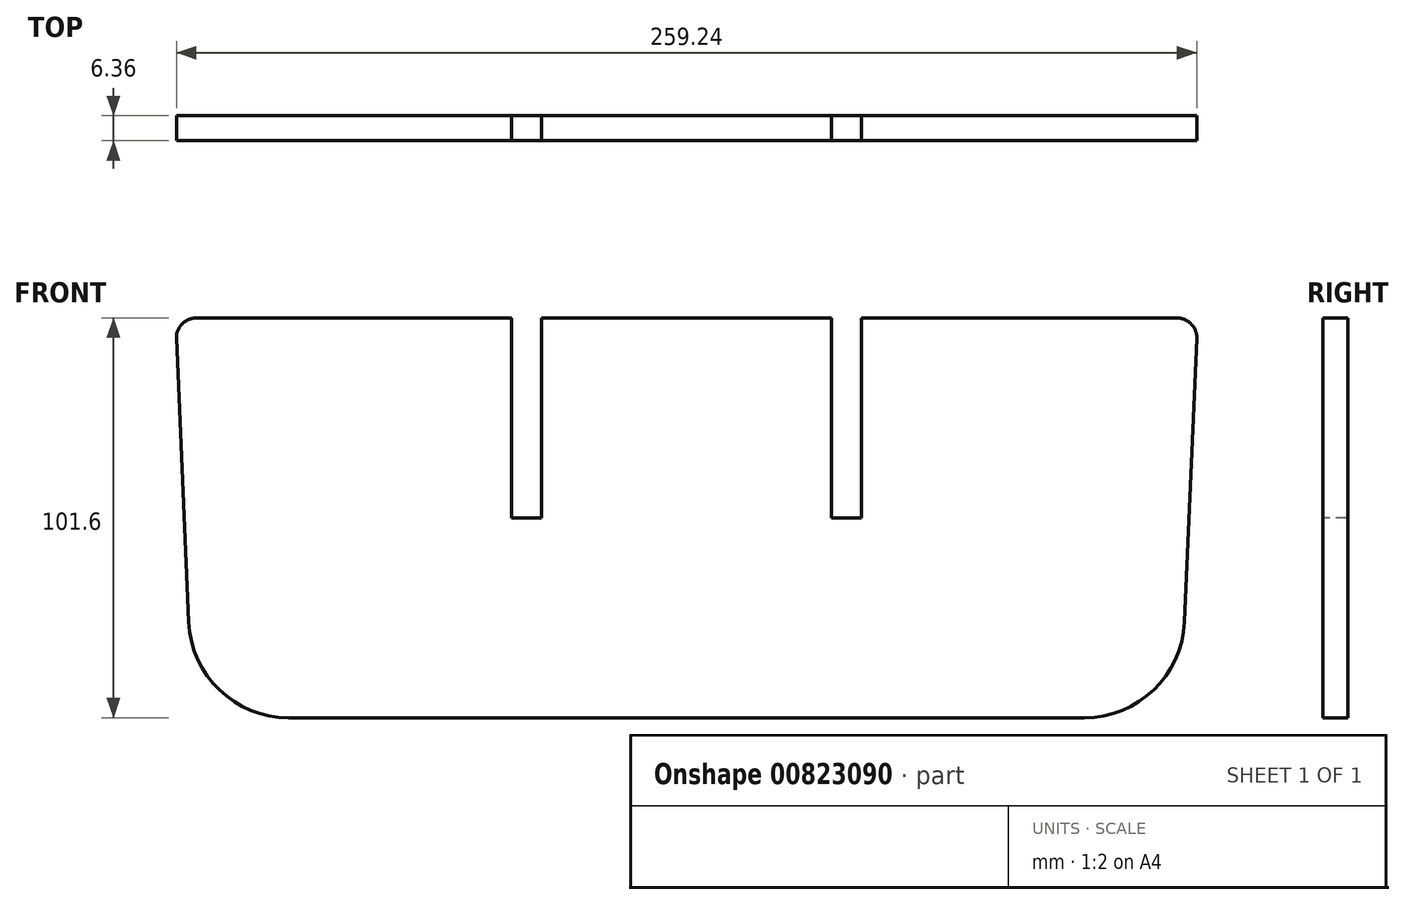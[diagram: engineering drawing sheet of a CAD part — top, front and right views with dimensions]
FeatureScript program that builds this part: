
annotation { "Feature Type Name" : "Feature", "Feature Type Description" : "" }
export const myFeature = defineFeature(function(context is Context, id is Id, definition is map)
    precondition{}
    {
        {
            var Q0;
            Q0=qCreatedBy(makeId("Front.planeOp"),FACE);
            var sketch = newSketch(context, id + "F0", { "sketchPlane" : qUnion([Q0])});
            skLineSegment(sketch, "E0", {"start": v(-129.85, 101.6) * mm, "end": v(-125.41, 0) * mm});
            skLineSegment(sketch, "E1", {"start": v(-125.41, 0) * mm, "end": v(125.41, 0) * mm});
            skLineSegment(sketch, "E2", {"start": v(125.41, 0) * mm, "end": v(129.85, 101.6) * mm});
            skLineSegment(sketch, "E3", {"start": v(129.85, 101.6) * mm, "end": v(-129.85, 101.6) * mm});
            skSolve(sketch);
        }
        {
            var Q0;
            Q0 = qSketchRegion(id + "F0", true);
            extrude(context, id + "F1", {"entities" : qUnion([Q0]), "endBound" : BoundingType.SYMMETRIC, "depth" : 6.35 * mm, "offsetDistance" : 25.4 * mm});
        }
        {
            var Q0;
            Q0=qCreatedBy(makeId("Front.planeOp"),FACE);
            var sketch = newSketch(context, id + "F2", { "sketchPlane" : qUnion([Q0])});
            skLineSegment(sketch, "E4", {"start": v(-40.64, 137.34) * mm, "end": v(-40.64, -20.45) * mm, "construction": true});
            skLineSegment(sketch, "E5.bottom", {"start": v(-36.83, 50.8) * mm, "end": v(-44.45, 50.8) * mm});
            skLineSegment(sketch, "E5.top", {"start": v(-36.83, 101.6) * mm, "end": v(-44.45, 101.6) * mm});
            skLineSegment(sketch, "E5.left", {"start": v(-36.83, 50.8) * mm, "end": v(-36.83, 101.6) * mm});
            skLineSegment(sketch, "E5.right", {"start": v(-44.45, 50.8) * mm, "end": v(-44.45, 101.6) * mm});
            skLineSegment(sketch, "E6.MirrorCS", {"start": v(36.83, 50.8) * mm, "end": v(44.45, 50.8) * mm});
            skLineSegment(sketch, "E7.MirrorCS", {"start": v(36.83, 101.6) * mm, "end": v(44.45, 101.6) * mm});
            skLineSegment(sketch, "E8.MirrorCS", {"start": v(36.83, 50.8) * mm, "end": v(36.83, 101.6) * mm});
            skLineSegment(sketch, "E9.MirrorCS", {"start": v(44.45, 50.8) * mm, "end": v(44.45, 101.6) * mm});
            skSolve(sketch);
        }
        {
            var Q0;
            Q0 = qSketchRegion(id + "F2", true);
            extrude(context, id + "F3", {"entities" : qUnion([Q0]), "operationType" : NewBodyOperationType.REMOVE, "endBound" : BoundingType.SYMMETRIC, "oppositeDirection" : true, "depth" : 25.4 * mm, "offsetDistance" : 25.4 * mm});
        }
        {
            var Q0;
            Q0=makeQuery(id+"F1.opExtrude","SWEPT_EDGE",EDGE,{"disambiguationData":[OSD([sQuery(id+"F0.wireOp",EDGE,"E0"),sQuery(id+"F0.wireOp",EDGE,"E1")])]});
            var Q1;
            Q1=makeQuery(id+"F1.opExtrude","SWEPT_EDGE",EDGE,{"disambiguationData":[OSD([sQuery(id+"F0.wireOp",EDGE,"E1"),sQuery(id+"F0.wireOp",EDGE,"E2")])]});
            fillet(context, id + "F4", {"entities" : qUnion([Q0, Q1]), "radius" : 25.4 * mm, "tangentPropagation" : true, "allowEdgeOverflow" : false});
        }
        {
            var Q0;
            Q0=makeQuery(id+"F1.opExtrude","SWEPT_EDGE",EDGE,{"disambiguationData":[OSD([sQuery(id+"F0.wireOp",EDGE,"E0"),sQuery(id+"F0.wireOp",EDGE,"E3")])]});
            var Q1;
            Q1=makeQuery(id+"F1.opExtrude","SWEPT_EDGE",EDGE,{"disambiguationData":[OSD([sQuery(id+"F0.wireOp",EDGE,"E2"),sQuery(id+"F0.wireOp",EDGE,"E3")])]});
            fillet(context, id + "F5", {"entities" : qUnion([Q0, Q1]), "radius" : 5.08 * mm, "tangentPropagation" : true, "allowEdgeOverflow" : false});
        }
    });
